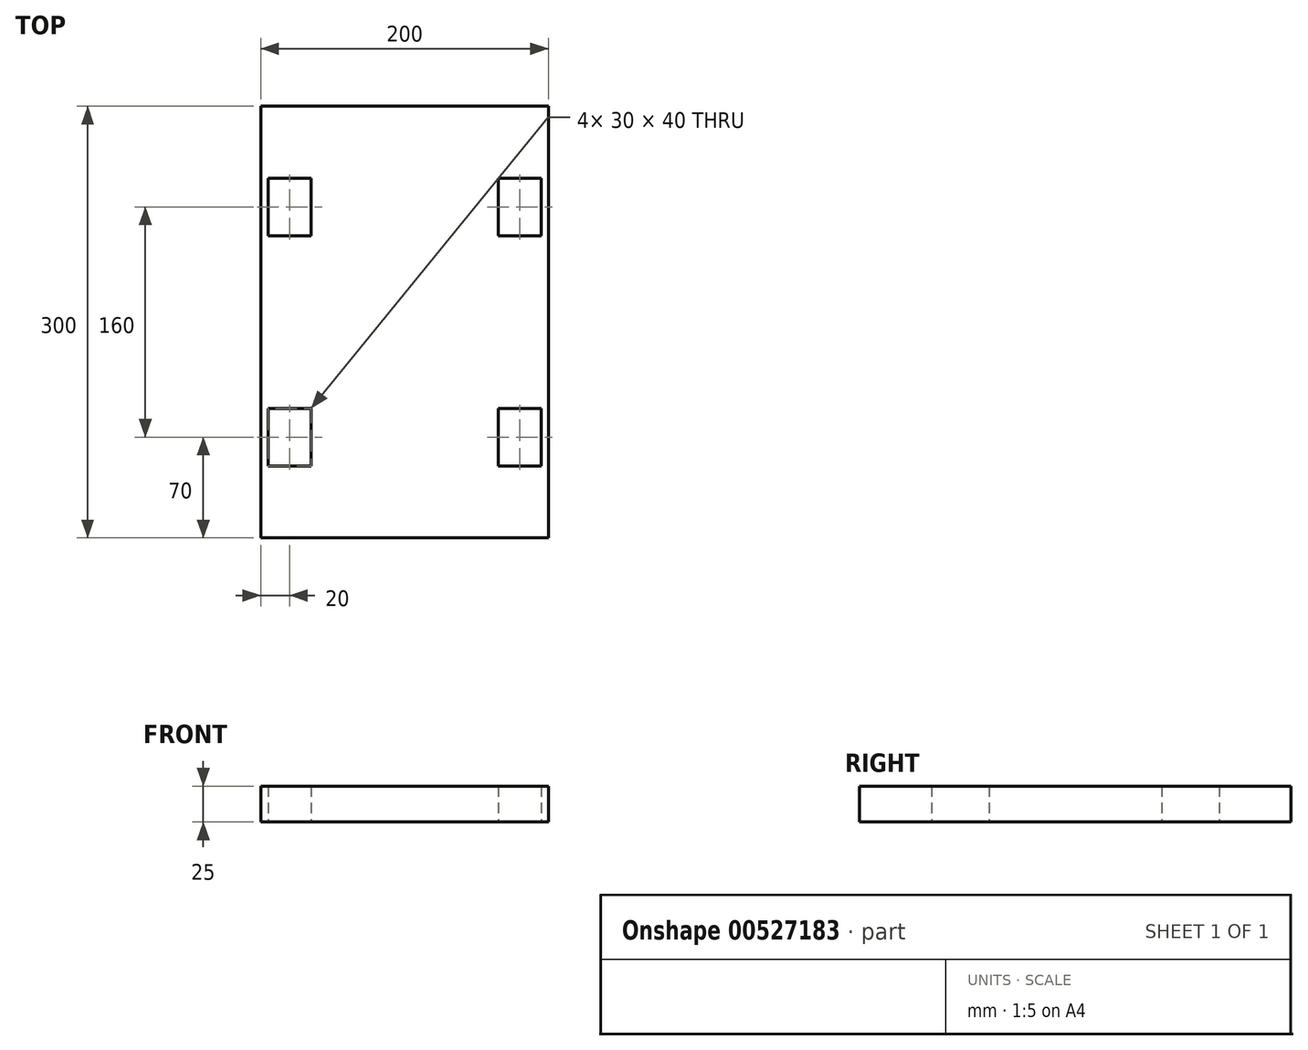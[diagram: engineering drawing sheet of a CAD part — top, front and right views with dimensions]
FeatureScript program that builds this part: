
annotation { "Feature Type Name" : "Feature", "Feature Type Description" : "" }
export const myFeature = defineFeature(function(context is Context, id is Id, definition is map)
    precondition{}
    {
        {
            var Q0;
            Q0=qCreatedBy(makeId("Top.planeOp"),FACE);
            var sketch = newSketch(context, id + "F0", { "sketchPlane" : qUnion([Q0])});
            skLineSegment(sketch, "E0.bottom", {"start": v(-100, 150) * mm, "end": v(100, 150) * mm});
            skLineSegment(sketch, "E0.top", {"start": v(-100, -150) * mm, "end": v(100, -150) * mm});
            skLineSegment(sketch, "E0.left", {"start": v(-100, 150) * mm, "end": v(-100, -150) * mm});
            skLineSegment(sketch, "E0.right", {"start": v(100, 150) * mm, "end": v(100, -150) * mm});
            skPoint(sketch, "E0.middle", {"position": v(0, 0) * mm});
            skLineSegment(sketch, "E1.bottom", {"start": v(-95, 100) * mm, "end": v(-65, 100) * mm});
            skLineSegment(sketch, "E1.top", {"start": v(-95, 60) * mm, "end": v(-65, 60) * mm});
            skLineSegment(sketch, "E1.left", {"start": v(-95, 100) * mm, "end": v(-95, 60) * mm});
            skLineSegment(sketch, "E1.right", {"start": v(-65, 100) * mm, "end": v(-65, 60) * mm});
            skLineSegment(sketch, "E2.0.1.0", {"start": v(-65, -60) * mm, "end": v(-65, -100) * mm});
            skLineSegment(sketch, "E2.0.1.1", {"start": v(-95, -60) * mm, "end": v(-65, -60) * mm});
            skLineSegment(sketch, "E2.0.1.2", {"start": v(-95, -100) * mm, "end": v(-65, -100) * mm});
            skLineSegment(sketch, "E2.0.1.3", {"start": v(-95, -60) * mm, "end": v(-95, -100) * mm});
            skLineSegment(sketch, "E2.1.0.0", {"start": v(95, 100) * mm, "end": v(95, 60) * mm});
            skLineSegment(sketch, "E2.1.0.1", {"start": v(65, 100) * mm, "end": v(95, 100) * mm});
            skLineSegment(sketch, "E2.1.0.2", {"start": v(65, 60) * mm, "end": v(95, 60) * mm});
            skLineSegment(sketch, "E2.1.0.3", {"start": v(65, 100) * mm, "end": v(65, 60) * mm});
            skLineSegment(sketch, "E2.1.1.0", {"start": v(95, -60) * mm, "end": v(95, -100) * mm});
            skLineSegment(sketch, "E2.1.1.1", {"start": v(65, -60) * mm, "end": v(95, -60) * mm});
            skLineSegment(sketch, "E2.1.1.2", {"start": v(65, -100) * mm, "end": v(95, -100) * mm});
            skLineSegment(sketch, "E2.1.1.3", {"start": v(65, -60) * mm, "end": v(65, -100) * mm});
            skLineSegment(sketch, "E2.direction1", {"start": v(-65, 60) * mm, "end": v(95, 60) * mm, "construction": true});
            skLineSegment(sketch, "E2.direction2", {"start": v(-65, 60) * mm, "end": v(-65, -100) * mm, "construction": true});
            skSolve(sketch);
        }
        {
            var Q0;
            Q0 = qSketchRegion(id + "F0", true);
            extrude(context, id + "F1", {"entities" : qUnion([Q0]), "depth" : 25 * mm, "offsetDistance" : 25 * mm});
        }
    });
